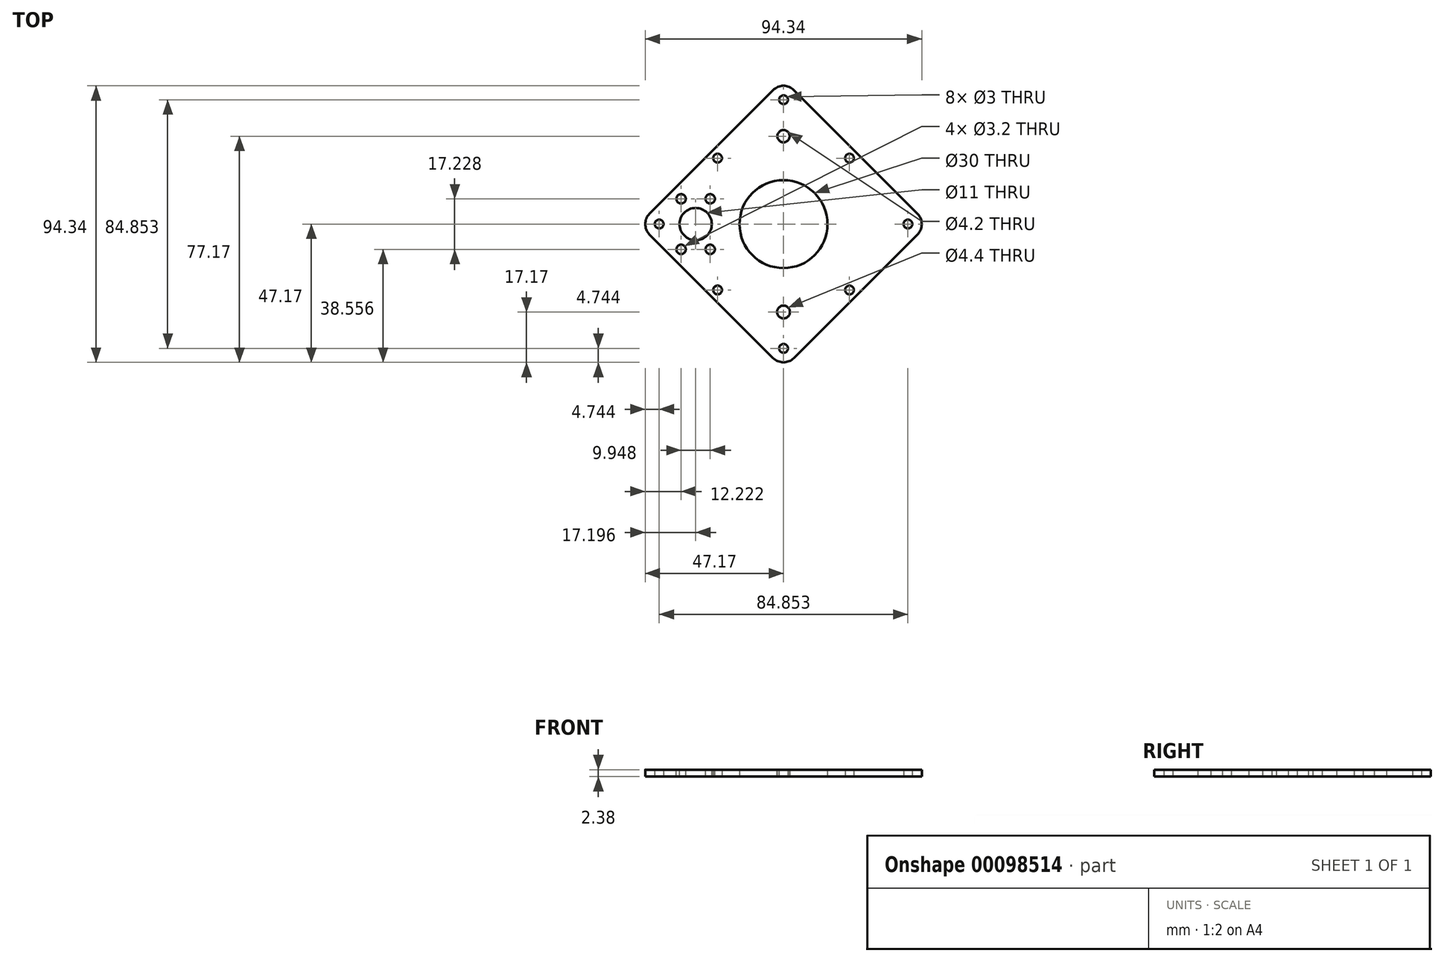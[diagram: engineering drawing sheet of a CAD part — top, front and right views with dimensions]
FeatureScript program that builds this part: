
annotation { "Feature Type Name" : "Feature", "Feature Type Description" : "" }
export const myFeature = defineFeature(function(context is Context, id is Id, definition is map)
    precondition{}
    {
        {
            var Q0;
            Q0=qCreatedBy(makeId("Top.planeOp"),FACE);
            var sketch = newSketch(context, id + "F0", { "sketchPlane" : qUnion([Q0])});
            skLineSegment(sketch, "E0", {"start": v(0, 0) * mm, "end": v(22.5, 0) * mm});
            skLineSegment(sketch, "E1", {"start": v(22.5, 0) * mm, "end": v(22.5, 22.5) * mm});
            skLineSegment(sketch, "E2", {"start": v(22.5, 22.5) * mm, "end": v(-22.5, 22.5) * mm});
            skLineSegment(sketch, "E3", {"start": v(-22.5, 22.5) * mm, "end": v(-22.5, -22.5) * mm});
            skLineSegment(sketch, "E4", {"start": v(-22.5, -22.5) * mm, "end": v(22.5, -22.5) * mm});
            skLineSegment(sketch, "E5", {"start": v(22.5, -22.5) * mm, "end": v(22.5, 0) * mm});
            skCircle(sketch, "E6", {"center": v(22.5, 22.5) * mm, "radius": 1.5 * mm});
            skCircle(sketch, "E7", {"center": v(22.5, -22.5) * mm, "radius": 1.5 * mm});
            skCircle(sketch, "E8", {"center": v(-22.5, -22.5) * mm, "radius": 1.5 * mm});
            skCircle(sketch, "E9", {"center": v(-22.5, 22.5) * mm, "radius": 1.5 * mm});
            skCircle(sketch, "E10", {"center": v(0, 0) * mm, "radius": 15 * mm});
            skLineSegment(sketch, "E11", {"start": v(0, 0) * mm, "end": v(21.21, 21.21) * mm});
            skCircle(sketch, "E12.cCircle", {"center": v(0, 0) * mm, "radius": 30 * mm, "construction": true});
            skLineSegment(sketch, "E12.0", {"start": v(0, 42.43) * mm, "end": v(42.43, 0) * mm});
            skLineSegment(sketch, "E12.1", {"start": v(42.43, 0) * mm, "end": v(0, -42.43) * mm});
            skLineSegment(sketch, "E12.2", {"start": v(0, -42.43) * mm, "end": v(-42.43, 0) * mm});
            skLineSegment(sketch, "E12.3", {"start": v(-42.43, 0) * mm, "end": v(0, 42.43) * mm});
            skPoint(sketch, "E12.0.midPoint", {"position": v(21.21, 21.21) * mm});
            skCircle(sketch, "E13", {"center": v(0, 42.43) * mm, "radius": 1.5 * mm});
            skCircle(sketch, "E14", {"center": v(42.43, 0) * mm, "radius": 1.5 * mm});
            skCircle(sketch, "E15", {"center": v(0, -42.43) * mm, "radius": 1.5 * mm});
            skCircle(sketch, "E16", {"center": v(-42.43, 0) * mm, "radius": 1.5 * mm});
            skPoint(sketch, "E17.0.midPoint", {"position": v(-47.93, 0) * mm});
            skLineSegment(sketch, "E18", {"start": v(22.5, 22.5) * mm, "end": v(24.57, 24.67) * mm});
            skLineSegment(sketch, "E19", {"start": v(-22.5, 22.5) * mm, "end": v(-24.62, 24.62) * mm});
            skLineSegment(sketch, "E20", {"start": v(22.5, -22.5) * mm, "end": v(24.62, -24.62) * mm});
            skLineSegment(sketch, "E21", {"start": v(-22.5, -22.5) * mm, "end": v(-24.62, -24.62) * mm});
            skCircle(sketch, "E22.cCircle", {"center": v(0, 0) * mm, "radius": 34.82 * mm, "construction": true});
            skLineSegment(sketch, "E22.0", {"start": v(-49.24, 0) * mm, "end": v(0, 49.24) * mm});
            skLineSegment(sketch, "E22.1", {"start": v(0, 49.24) * mm, "end": v(49.24, 0) * mm});
            skLineSegment(sketch, "E22.2", {"start": v(49.24, 0) * mm, "end": v(0, -49.24) * mm});
            skLineSegment(sketch, "E22.3", {"start": v(0, -49.24) * mm, "end": v(-49.24, 0) * mm});
            skPoint(sketch, "E22.0.midPoint", {"position": v(-24.62, 24.62) * mm});
            skSolve(sketch);
        }
        {
            var Q0;
            {var subQ5=sQuery(id+"F0.wireOp",EDGE,"E1");var subQ7=sQuery(id+"F0.wireOp",EDGE,"E6");var subQ8=makeQuery(id+"F0.imprint","INTERSECT",VERTEX,{"derivedFrom":[subQ5,subQ7]});Q0=makeQuery(id+"F0.imprint","IMPRINT",FACE,{"disambiguationData":[TD([[makeQuery(id+"F0.imprint","IMPRINT",EDGE,{"disambiguationData":[TD([[subQ8,1.0]])],"derivedFrom":subQ7}),-1.0]])]});}
            var Q1;
            {var subQ0=sQuery(id+"F0.wireOp",EDGE,"E17.1");Q1=makeQuery(id+"F0.imprint","IMPRINT",FACE,{"disambiguationData":[TD([[makeQuery(id+"F0.imprint","IMPRINT",EDGE,{"derivedFrom":subQ0}),-1.0]])]});}
            var Q2;
            {var subQ6=sQuery(id+"F0.wireOp",EDGE,"E2");var subQ19=sQuery(id+"F0.wireOp",EDGE,"E6");var subQ20=makeQuery(id+"F0.imprint","INTERSECT",VERTEX,{"derivedFrom":[subQ6,subQ19]});Q2=makeQuery(id+"F0.imprint","IMPRINT",FACE,{"disambiguationData":[TD([[makeQuery(id+"F0.imprint","IMPRINT",EDGE,{"disambiguationData":[TD([[subQ20,-1.0]])],"derivedFrom":subQ6}),1.0]])]});}
            var Q3;
            {var subQ5=sQuery(id+"F0.wireOp",EDGE,"E9");var subQ6=sQuery(id+"F0.wireOp",EDGE,"E3");var subQ7=makeQuery(id+"F0.imprint","INTERSECT",VERTEX,{"derivedFrom":[subQ6,subQ5]});Q3=makeQuery(id+"F0.imprint","IMPRINT",FACE,{"disambiguationData":[TD([[makeQuery(id+"F0.imprint","IMPRINT",EDGE,{"disambiguationData":[TD([[subQ7,-1.0]])],"derivedFrom":subQ6}),-1.0]])]});}
            var Q4;
            {var subQ5=sQuery(id+"F0.wireOp",EDGE,"E4");var subQ7=sQuery(id+"F0.wireOp",EDGE,"E8");var subQ8=makeQuery(id+"F0.imprint","INTERSECT",VERTEX,{"derivedFrom":[subQ5,subQ7]});Q4=makeQuery(id+"F0.imprint","IMPRINT",FACE,{"disambiguationData":[TD([[makeQuery(id+"F0.imprint","IMPRINT",EDGE,{"disambiguationData":[TD([[subQ8,-1.0]])],"derivedFrom":subQ5}),-1.0]])]});}
            var Q5;
            {var subQ5=sQuery(id+"F0.wireOp",EDGE,"E1");var subQ7=sQuery(id+"F0.wireOp",EDGE,"E6");var subQ8=makeQuery(id+"F0.imprint","INTERSECT",VERTEX,{"derivedFrom":[subQ5,subQ7]});Q5=makeQuery(id+"F0.imprint","IMPRINT",FACE,{"disambiguationData":[TD([[makeQuery(id+"F0.imprint","IMPRINT",EDGE,{"disambiguationData":[TD([[subQ8,-1.0]])],"derivedFrom":subQ7}),-1.0]])]});}
            var Q6;
            {var subQ1=sQuery(id+"F0.wireOp",EDGE,"E6");var subQ6=sQuery(id+"F0.wireOp",EDGE,"E2");var subQ11=makeQuery(id+"F0.imprint","INTERSECT",VERTEX,{"derivedFrom":[subQ6,subQ1]});Q6=makeQuery(id+"F0.imprint","IMPRINT",FACE,{"disambiguationData":[TD([[makeQuery(id+"F0.imprint","IMPRINT",EDGE,{"disambiguationData":[TD([[subQ11,-1.0]])],"derivedFrom":subQ6}),-1.0]])]});}
            var Q7;
            {var subQ0=sQuery(id+"F0.wireOp",EDGE,"E12.3");var subQ1=sQuery(id+"F0.wireOp",EDGE,"E3");var subQ2=makeQuery(id+"F0.imprint","INTERSECT",VERTEX,{"derivedFrom":[subQ1,subQ0]});Q7=makeQuery(id+"F0.imprint","IMPRINT",FACE,{"disambiguationData":[TD([[makeQuery(id+"F0.imprint","IMPRINT",EDGE,{"disambiguationData":[TD([[subQ2,-1.0]])],"derivedFrom":subQ1}),-1.0]])]});}
            var Q8;
            {var subQ0=sQuery(id+"F0.wireOp",EDGE,"E12.0");var subQ1=sQuery(id+"F0.wireOp",EDGE,"E2");var subQ2=makeQuery(id+"F0.imprint","INTERSECT",VERTEX,{"derivedFrom":[subQ1,subQ0]});Q8=makeQuery(id+"F0.imprint","IMPRINT",FACE,{"disambiguationData":[TD([[makeQuery(id+"F0.imprint","IMPRINT",EDGE,{"disambiguationData":[TD([[subQ2,-1.0]])],"derivedFrom":subQ1}),-1.0]])]});}
            var Q9;
            {var subQ5=sQuery(id+"F0.wireOp",EDGE,"E1");var subQ7=sQuery(id+"F0.wireOp",EDGE,"E12.0");var subQ8=makeQuery(id+"F0.imprint","INTERSECT",VERTEX,{"derivedFrom":[subQ5,subQ7]});Q9=makeQuery(id+"F0.imprint","IMPRINT",FACE,{"disambiguationData":[TD([[makeQuery(id+"F0.imprint","IMPRINT",EDGE,{"disambiguationData":[TD([[subQ8,-1.0]])],"derivedFrom":subQ7}),-1.0]])]});}
            var Q10;
            {var subQ0=sQuery(id+"F0.wireOp",EDGE,"E12.2");var subQ1=sQuery(id+"F0.wireOp",EDGE,"E4");var subQ2=makeQuery(id+"F0.imprint","INTERSECT",VERTEX,{"derivedFrom":[subQ1,subQ0]});Q10=makeQuery(id+"F0.imprint","IMPRINT",FACE,{"disambiguationData":[TD([[makeQuery(id+"F0.imprint","IMPRINT",EDGE,{"disambiguationData":[TD([[subQ2,-1.0]])],"derivedFrom":subQ1}),-1.0]])]});}
            var Q11;
            {var subQ0=sQuery(id+"F0.wireOp",EDGE,"E12.0");var subQ16=sQuery(id+"F0.wireOp",EDGE,"E2");var subQ17=makeQuery(id+"F0.imprint","INTERSECT",VERTEX,{"derivedFrom":[subQ16,subQ0]});Q11=makeQuery(id+"F0.imprint","IMPRINT",FACE,{"disambiguationData":[TD([[makeQuery(id+"F0.imprint","IMPRINT",EDGE,{"disambiguationData":[TD([[subQ17,-1.0]])],"derivedFrom":subQ16}),1.0]])]});}
            var Q12;
            {var subQ3=sQuery(id+"F0.wireOp",EDGE,"E10");var subQ5=sQuery(id+"F0.wireOp",EDGE,"E0");var subQ6=makeQuery(id+"F0.imprint","INTERSECT",VERTEX,{"derivedFrom":[subQ5,subQ3]});Q12=makeQuery(id+"F0.imprint","IMPRINT",FACE,{"disambiguationData":[TD([[makeQuery(id+"F0.imprint","IMPRINT",EDGE,{"disambiguationData":[TD([[subQ6,-1.0]])],"derivedFrom":subQ3}),-1.0]])]});}
            var Q13;
            {var subQ0=sQuery(id+"F0.wireOp",EDGE,"E12.2");var subQ1=sQuery(id+"F0.wireOp",EDGE,"E3");var subQ2=makeQuery(id+"F0.imprint","INTERSECT",VERTEX,{"derivedFrom":[subQ1,subQ0]});Q13=makeQuery(id+"F0.imprint","IMPRINT",FACE,{"disambiguationData":[TD([[makeQuery(id+"F0.imprint","IMPRINT",EDGE,{"disambiguationData":[TD([[subQ2,-1.0]])],"derivedFrom":subQ1}),1.0]])]});}
            var Q14;
            {var subQ0=sQuery(id+"F0.wireOp",EDGE,"E12.3");var subQ1=sQuery(id+"F0.wireOp",EDGE,"E2");var subQ2=makeQuery(id+"F0.imprint","INTERSECT",VERTEX,{"derivedFrom":[subQ1,subQ0]});Q14=makeQuery(id+"F0.imprint","IMPRINT",FACE,{"disambiguationData":[TD([[makeQuery(id+"F0.imprint","IMPRINT",EDGE,{"disambiguationData":[TD([[subQ2,-1.0]])],"derivedFrom":subQ1}),1.0]])]});}
            var Q15;
            {var subQ0=sQuery(id+"F0.wireOp",EDGE,"E12.1");var subQ1=sQuery(id+"F0.wireOp",EDGE,"E4");var subQ2=makeQuery(id+"F0.imprint","INTERSECT",VERTEX,{"derivedFrom":[subQ1,subQ0]});Q15=makeQuery(id+"F0.imprint","IMPRINT",FACE,{"disambiguationData":[TD([[makeQuery(id+"F0.imprint","IMPRINT",EDGE,{"disambiguationData":[TD([[subQ2,-1.0]])],"derivedFrom":subQ1}),1.0]])]});}
            extrude(context, id + "F1", {"entities" : qUnion([Q0, Q1, Q2, Q3, Q4, Q5, Q6, Q7, Q8, Q9, Q10, Q11, Q12, Q13, Q14, Q15]), "depth" : 2.38 * mm});
        }
        {
            var Q0;
            Q0=makeQuery(id+"F1.opExtrude","SWEPT_EDGE",EDGE,{"disambiguationData":[OSD([sQuery(id+"F0.wireOp",EDGE,"E22.2"),sQuery(id+"F0.wireOp",EDGE,"E22.3")])]});
            var Q1;
            Q1=makeQuery(id+"F1.opExtrude","SWEPT_EDGE",EDGE,{"disambiguationData":[OSD([sQuery(id+"F0.wireOp",EDGE,"E22.1"),sQuery(id+"F0.wireOp",EDGE,"E22.2")])]});
            var Q2;
            Q2=makeQuery(id+"F1.opExtrude","SWEPT_EDGE",EDGE,{"disambiguationData":[OSD([sQuery(id+"F0.wireOp",EDGE,"E22.0"),sQuery(id+"F0.wireOp",EDGE,"E22.1")])]});
            var Q3;
            Q3=makeQuery(id+"F1.opExtrude","SWEPT_EDGE",EDGE,{"disambiguationData":[OSD([sQuery(id+"F0.wireOp",EDGE,"E22.0"),sQuery(id+"F0.wireOp",EDGE,"E22.3")])]});
            fillet(context, id + "F2", {"entities" : qUnion([Q0, Q1, Q2, Q3]), "radius" : 5 * mm, "tangentPropagation" : true, "allowEdgeOverflow" : false});
        }
        {
            var Q0;
            Q0=makeQuery(id+"F1.opExtrude","CAP_FACE",FACE,{"disambiguationData":[OSD([sQuery(id+"F0.wireOp",EDGE,"E10"),sQuery(id+"F0.wireOp",EDGE,"E13"),sQuery(id+"F0.wireOp",EDGE,"E14"),sQuery(id+"F0.wireOp",EDGE,"E15"),sQuery(id+"F0.wireOp",EDGE,"E16"),sQuery(id+"F0.wireOp",EDGE,"E22.0"),sQuery(id+"F0.wireOp",EDGE,"E22.1"),sQuery(id+"F0.wireOp",EDGE,"E22.2"),sQuery(id+"F0.wireOp",EDGE,"E22.3")])],"isStart":false});
            var sketch = newSketch(context, id + "F3", { "sketchPlane" : qUnion([Q0])});
            skLineSegment(sketch, "E23", {"start": v(-29.97, 8.61) * mm, "end": v(-34.95, 8.61) * mm, "construction": true});
            skLineSegment(sketch, "E24", {"start": v(-29.97, -8.61) * mm, "end": v(-25, -8.61) * mm});
            skLineSegment(sketch, "E25", {"start": v(-29.97, 8.61) * mm, "end": v(-25, 8.61) * mm});
            skLineSegment(sketch, "E26", {"start": v(-34.95, -8.61) * mm, "end": v(-29.97, -8.61) * mm});
            skLineSegment(sketch, "E27", {"start": v(-34.95, 8.61) * mm, "end": v(-29.97, 8.61) * mm});
            skLineSegment(sketch, "E28", {"start": v(-25, -8.61) * mm, "end": v(-25, 8.61) * mm});
            skCircle(sketch, "E29", {"center": v(-34.95, 8.61) * mm, "radius": 1.6 * mm});
            skCircle(sketch, "E30", {"center": v(-25, 8.61) * mm, "radius": 1.6 * mm});
            skCircle(sketch, "E31", {"center": v(-25, -8.61) * mm, "radius": 1.6 * mm});
            skCircle(sketch, "E32", {"center": v(-34.95, -8.61) * mm, "radius": 1.6 * mm});
            skLineSegment(sketch, "E33", {"start": v(-25, 0) * mm, "end": v(-34.95, 0) * mm});
            skLineSegment(sketch, "E34", {"start": v(-34.95, 0) * mm, "end": v(-29.97, 0) * mm});
            skCircle(sketch, "E35", {"center": v(-29.97, 0) * mm, "radius": 5.5 * mm});
            skCircle(sketch, "E36", {"center": v(0, 0) * mm, "radius": 15.25 * mm});
            skLineSegment(sketch, "E37", {"start": v(-25, 0) * mm, "end": v(0, 0) * mm});
            skLineSegment(sketch, "E38", {"start": v(-34.95, 8.61) * mm, "end": v(-34.95, 0) * mm});
            skLineSegment(sketch, "E39", {"start": v(-34.95, 0) * mm, "end": v(-34.95, -8.61) * mm});
            skSolve(sketch);
        }
        {
            var Q0;
            {var subQ0=sQuery(id+"F3.wireOp",EDGE,"E28");var subQ1=sQuery(id+"F3.wireOp",EDGE,"E24");var subQ2=makeQuery(id+"F3.imprint","INTERSECT",VERTEX,{"derivedFrom":[subQ1,subQ0]});Q0=makeQuery(id+"F3.imprint","IMPRINT",FACE,{"disambiguationData":[TD([[makeQuery(id+"F3.imprint","IMPRINT",EDGE,{"disambiguationData":[TD([[subQ2,1.0]])],"derivedFrom":subQ1}),1.0]])]});}
            var Q1;
            {var subQ0=sQuery(id+"F3.wireOp",EDGE,"E28");var subQ1=sQuery(id+"F3.wireOp",EDGE,"E24");var subQ2=makeQuery(id+"F3.imprint","INTERSECT",VERTEX,{"derivedFrom":[subQ1,subQ0]});Q1=makeQuery(id+"F3.imprint","IMPRINT",FACE,{"disambiguationData":[TD([[makeQuery(id+"F3.imprint","IMPRINT",EDGE,{"disambiguationData":[TD([[subQ2,1.0]])],"derivedFrom":subQ1}),-1.0]])]});}
            var Q2;
            {var subQ0=sQuery(id+"F3.wireOp",EDGE,"E28");var subQ1=sQuery(id+"F3.wireOp",EDGE,"E25");var subQ2=makeQuery(id+"F3.imprint","INTERSECT",VERTEX,{"derivedFrom":[subQ1,subQ0]});Q2=makeQuery(id+"F3.imprint","IMPRINT",FACE,{"disambiguationData":[TD([[makeQuery(id+"F3.imprint","IMPRINT",EDGE,{"disambiguationData":[TD([[subQ2,1.0]])],"derivedFrom":subQ1}),-1.0]])]});}
            var Q3;
            {var subQ0=sQuery(id+"F3.wireOp",EDGE,"E28");var subQ1=sQuery(id+"F3.wireOp",EDGE,"E25");var subQ2=makeQuery(id+"F3.imprint","INTERSECT",VERTEX,{"derivedFrom":[subQ1,subQ0]});Q3=makeQuery(id+"F3.imprint","IMPRINT",FACE,{"disambiguationData":[TD([[makeQuery(id+"F3.imprint","IMPRINT",EDGE,{"disambiguationData":[TD([[subQ2,1.0]])],"derivedFrom":subQ1}),1.0]])]});}
            var Q4;
            {var subQ0=sQuery(id+"F3.wireOp",EDGE,"E27");var subQ1=sQuery(id+"F3.wireOp",EDGE,"d6gp2X51-tT9r-q6k6-2jgA-M0tPCtTGG1G5");var subQ2=makeQuery(id+"F3.imprint","INTERSECT",VERTEX,{"derivedFrom":[subQ1,subQ0]});Q4=makeQuery(id+"F3.imprint","IMPRINT",FACE,{"disambiguationData":[TD([[makeQuery(id+"F3.imprint","IMPRINT",EDGE,{"disambiguationData":[TD([[subQ2,-1.0]])],"derivedFrom":subQ1}),-1.0]])]});}
            var Q5;
            {var subQ0=sQuery(id+"F3.wireOp",EDGE,"E27");var subQ1=sQuery(id+"F3.wireOp",EDGE,"d6gp2X51-tT9r-q6k6-2jgA-M0tPCtTGG1G5");var subQ2=makeQuery(id+"F3.imprint","INTERSECT",VERTEX,{"derivedFrom":[subQ1,subQ0]});Q5=makeQuery(id+"F3.imprint","IMPRINT",FACE,{"disambiguationData":[TD([[makeQuery(id+"F3.imprint","IMPRINT",EDGE,{"disambiguationData":[TD([[subQ2,-1.0]])],"derivedFrom":subQ1}),1.0]])]});}
            var Q6;
            {var subQ0=sQuery(id+"F3.wireOp",EDGE,"E26");var subQ1=sQuery(id+"F3.wireOp",EDGE,"d6gp2X51-tT9r-q6k6-2jgA-M0tPCtTGG1G5");var subQ2=makeQuery(id+"F3.imprint","INTERSECT",VERTEX,{"derivedFrom":[subQ1,subQ0]});Q6=makeQuery(id+"F3.imprint","IMPRINT",FACE,{"disambiguationData":[TD([[makeQuery(id+"F3.imprint","IMPRINT",EDGE,{"disambiguationData":[TD([[subQ2,1.0]])],"derivedFrom":subQ1}),1.0]])]});}
            var Q7;
            {var subQ0=sQuery(id+"F3.wireOp",EDGE,"E26");var subQ1=sQuery(id+"F3.wireOp",EDGE,"d6gp2X51-tT9r-q6k6-2jgA-M0tPCtTGG1G5");var subQ2=makeQuery(id+"F3.imprint","INTERSECT",VERTEX,{"derivedFrom":[subQ1,subQ0]});Q7=makeQuery(id+"F3.imprint","IMPRINT",FACE,{"disambiguationData":[TD([[makeQuery(id+"F3.imprint","IMPRINT",EDGE,{"disambiguationData":[TD([[subQ2,1.0]])],"derivedFrom":subQ1}),-1.0]])]});}
            var Q8;
            {var subQ1=sQuery(id+"F3.wireOp",EDGE,"F08VXF3O-IFnZ-9qwD-Zmf6-qOkJdKaSuWAb");var subQ3=sQuery(id+"F3.wireOp",EDGE,"E35");var subQ4=makeQuery(id+"F3.imprint","INTERSECT",VERTEX,{"disambiguationData":[OD(0.0)],"derivedFrom":[subQ1,subQ3]});Q8=makeQuery(id+"F3.imprint","IMPRINT",FACE,{"disambiguationData":[TD([[makeQuery(id+"F3.imprint","IMPRINT",EDGE,{"disambiguationData":[TD([[subQ4,1.0]])],"derivedFrom":subQ3}),1.0]])]});}
            var Q9;
            {var subQ1=sQuery(id+"F3.wireOp",EDGE,"F08VXF3O-IFnZ-9qwD-Zmf6-qOkJdKaSuWAb");var subQ3=sQuery(id+"F3.wireOp",EDGE,"E35");var subQ4=makeQuery(id+"F3.imprint","INTERSECT",VERTEX,{"disambiguationData":[OD(0.0)],"derivedFrom":[subQ1,subQ3]});Q9=makeQuery(id+"F3.imprint","IMPRINT",FACE,{"disambiguationData":[TD([[makeQuery(id+"F3.imprint","IMPRINT",EDGE,{"disambiguationData":[TD([[subQ4,-1.0]])],"derivedFrom":subQ3}),1.0]])]});}
            var Q10;
            {var subQ1=sQuery(id+"F3.wireOp",EDGE,"F08VXF3O-IFnZ-9qwD-Zmf6-qOkJdKaSuWAb");var subQ3=sQuery(id+"F3.wireOp",EDGE,"E35");var subQ4=makeQuery(id+"F3.imprint","INTERSECT",VERTEX,{"disambiguationData":[OD(1.0)],"derivedFrom":[subQ1,subQ3]});Q10=makeQuery(id+"F3.imprint","IMPRINT",FACE,{"disambiguationData":[TD([[makeQuery(id+"F3.imprint","IMPRINT",EDGE,{"disambiguationData":[TD([[subQ4,1.0]])],"derivedFrom":subQ3}),1.0]])]});}
            var Q11;
            {var subQ1=sQuery(id+"F3.wireOp",EDGE,"F08VXF3O-IFnZ-9qwD-Zmf6-qOkJdKaSuWAb");var subQ3=sQuery(id+"F3.wireOp",EDGE,"E35");var subQ4=makeQuery(id+"F3.imprint","INTERSECT",VERTEX,{"disambiguationData":[OD(1.0)],"derivedFrom":[subQ1,subQ3]});Q11=makeQuery(id+"F3.imprint","IMPRINT",FACE,{"disambiguationData":[TD([[makeQuery(id+"F3.imprint","IMPRINT",EDGE,{"disambiguationData":[TD([[subQ4,-1.0]])],"derivedFrom":subQ3}),1.0]])]});}
            var Q12;
            {var subQ6=sQuery(id+"F3.wireOp",EDGE,"E33");Q12=makeQuery(id+"F3.imprint","IMPRINT",FACE,{"disambiguationData":[TD([[makeQuery(id+"F3.imprint","IMPRINT",EDGE,{"derivedFrom":subQ6}),-1.0]])]});}
            var Q13;
            {var subQ0=sQuery(id+"F3.wireOp",EDGE,"E33");Q13=makeQuery(id+"F3.imprint","IMPRINT",FACE,{"disambiguationData":[TD([[makeQuery(id+"F3.imprint","IMPRINT",EDGE,{"derivedFrom":subQ0}),1.0]])]});}
            var Q14;
            {var subQ0=sQuery(id+"F3.wireOp",EDGE,"E38");var subQ1=sQuery(id+"F3.wireOp",EDGE,"E27");var subQ2=makeQuery(id+"F3.imprint","INTERSECT",VERTEX,{"derivedFrom":[subQ1,subQ0]});Q14=makeQuery(id+"F3.imprint","IMPRINT",FACE,{"disambiguationData":[TD([[makeQuery(id+"F3.imprint","IMPRINT",EDGE,{"disambiguationData":[TD([[subQ2,-1.0]])],"derivedFrom":subQ1}),1.0]])]});}
            var Q15;
            {var subQ0=sQuery(id+"F3.wireOp",EDGE,"E38");var subQ1=sQuery(id+"F3.wireOp",EDGE,"E35");var subQ2=makeQuery(id+"F3.imprint","INTERSECT",VERTEX,{"derivedFrom":[subQ1,subQ0]});Q15=makeQuery(id+"F3.imprint","IMPRINT",FACE,{"disambiguationData":[TD([[makeQuery(id+"F3.imprint","IMPRINT",EDGE,{"disambiguationData":[TD([[subQ2,-1.0]])],"derivedFrom":subQ1}),1.0]])]});}
            var Q16;
            {var subQ0=sQuery(id+"F3.wireOp",EDGE,"E39");var subQ1=sQuery(id+"F3.wireOp",EDGE,"E26");var subQ2=makeQuery(id+"F3.imprint","INTERSECT",VERTEX,{"derivedFrom":[subQ1,subQ0]});Q16=makeQuery(id+"F3.imprint","IMPRINT",FACE,{"disambiguationData":[TD([[makeQuery(id+"F3.imprint","IMPRINT",EDGE,{"disambiguationData":[TD([[subQ2,-1.0]])],"derivedFrom":subQ1}),-1.0]])]});}
            var Q17;
            {var subQ0=sQuery(id+"F3.wireOp",EDGE,"E39");var subQ1=sQuery(id+"F3.wireOp",EDGE,"E26");var subQ2=makeQuery(id+"F3.imprint","INTERSECT",VERTEX,{"derivedFrom":[subQ1,subQ0]});Q17=makeQuery(id+"F3.imprint","IMPRINT",FACE,{"disambiguationData":[TD([[makeQuery(id+"F3.imprint","IMPRINT",EDGE,{"disambiguationData":[TD([[subQ2,-1.0]])],"derivedFrom":subQ1}),1.0]])]});}
            var Q18;
            {var subQ0=sQuery(id+"F3.wireOp",EDGE,"E38");var subQ1=sQuery(id+"F3.wireOp",EDGE,"E27");var subQ2=makeQuery(id+"F3.imprint","INTERSECT",VERTEX,{"derivedFrom":[subQ1,subQ0]});Q18=makeQuery(id+"F3.imprint","IMPRINT",FACE,{"disambiguationData":[TD([[makeQuery(id+"F3.imprint","IMPRINT",EDGE,{"disambiguationData":[TD([[subQ2,-1.0]])],"derivedFrom":subQ1}),-1.0]])]});}
            extrude(context, id + "F4", {"entities" : qUnion([Q0, Q1, Q2, Q3, Q4, Q5, Q6, Q7, Q8, Q9, Q10, Q11, Q12, Q13, Q14, Q15, Q16, Q17, Q18]), "operationType" : NewBodyOperationType.REMOVE, "oppositeDirection" : true, "depth" : 25 * mm});
        }
        {
            var Q0;
            Q0=makeQuery(id+"F1.opExtrude","CAP_FACE",FACE,{"disambiguationData":[OSD([sQuery(id+"F0.wireOp",EDGE,"E6"),sQuery(id+"F0.wireOp",EDGE,"E7"),sQuery(id+"F0.wireOp",EDGE,"E8"),sQuery(id+"F0.wireOp",EDGE,"E9"),sQuery(id+"F0.wireOp",EDGE,"E10"),sQuery(id+"F0.wireOp",EDGE,"E13"),sQuery(id+"F0.wireOp",EDGE,"E14"),sQuery(id+"F0.wireOp",EDGE,"E15"),sQuery(id+"F0.wireOp",EDGE,"E16"),sQuery(id+"F0.wireOp",EDGE,"E22.0"),sQuery(id+"F0.wireOp",EDGE,"E22.1"),sQuery(id+"F0.wireOp",EDGE,"E22.2"),sQuery(id+"F0.wireOp",EDGE,"E22.3")])],"isStart":false});
            var sketch = newSketch(context, id + "F5", { "sketchPlane" : qUnion([Q0])});
            skLineSegment(sketch, "E40", {"start": v(0, 0) * mm, "end": v(7.35, 0) * mm});
            skLineSegment(sketch, "E41", {"start": v(0, 0) * mm, "end": v(0, -30) * mm});
            skCircle(sketch, "E42", {"center": v(0, -30) * mm, "radius": 2.2 * mm});
            skLineSegment(sketch, "E43", {"start": v(0, 0) * mm, "end": v(0, 30) * mm});
            skCircle(sketch, "E44", {"center": v(0, 30) * mm, "radius": 2.1 * mm});
            skSolve(sketch);
        }
        {
            var Q0;
            Q0=makeQuery(id+"F5.imprint","IMPRINT",FACE,{"disambiguationData":[TD([[makeQuery(id+"F5.imprint","IMPRINT",EDGE,{"derivedFrom":sQuery(id+"F5.wireOp",EDGE,"E42")}),1.0]])]});
            var Q1;
            Q1=makeQuery(id+"F5.imprint","IMPRINT",FACE,{"disambiguationData":[TD([[makeQuery(id+"F5.imprint","IMPRINT",EDGE,{"derivedFrom":sQuery(id+"F5.wireOp",EDGE,"E44")}),1.0]])]});
            extrude(context, id + "F6", {"entities" : qUnion([Q0, Q1]), "operationType" : NewBodyOperationType.REMOVE, "oppositeDirection" : true, "depth" : 25 * mm});
        }
    });
